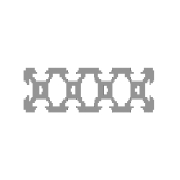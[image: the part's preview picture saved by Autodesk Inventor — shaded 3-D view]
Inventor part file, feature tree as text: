
AUTODESK INVENTOR PART (.ipt)
format: ipt  version: 2013 (Build 170138000, 138)  size: 278,016 bytes
history: native  units: mm
features: other x4, sketch x2, plane x1
ambient origin geometry x8: Origin, YZ Plane, XZ Plane, XY Plane, X Axis, Y Axis, Z Axis, Center Point
bodies: Solid1 (feature_tree), Body (feature_tree)
feature tree (7):
  other  "Driven Length"
  other  "Frame Generator"
  other  "Start Plane"
  other  "End Plane"
  sketch  "Sketch10"  dims[d0=10.0mm]
  plane  "Work Plane7"
  sketch  "Sketch11"  dims[d1=10.0mm d2=10.0mm d3=4.2mm d4=1.5mm d5=45.0deg d6=1.64mm d7=1.8mm d8=10.0mm d9=2.84mm d11=135.0deg d12=1.96mm d13=5.68mm d14=2.0mm d17=-0.0mm d18=475.0mm d19=0.13mm d20=0.0mm d29=90.0deg d22=475.0mm]
